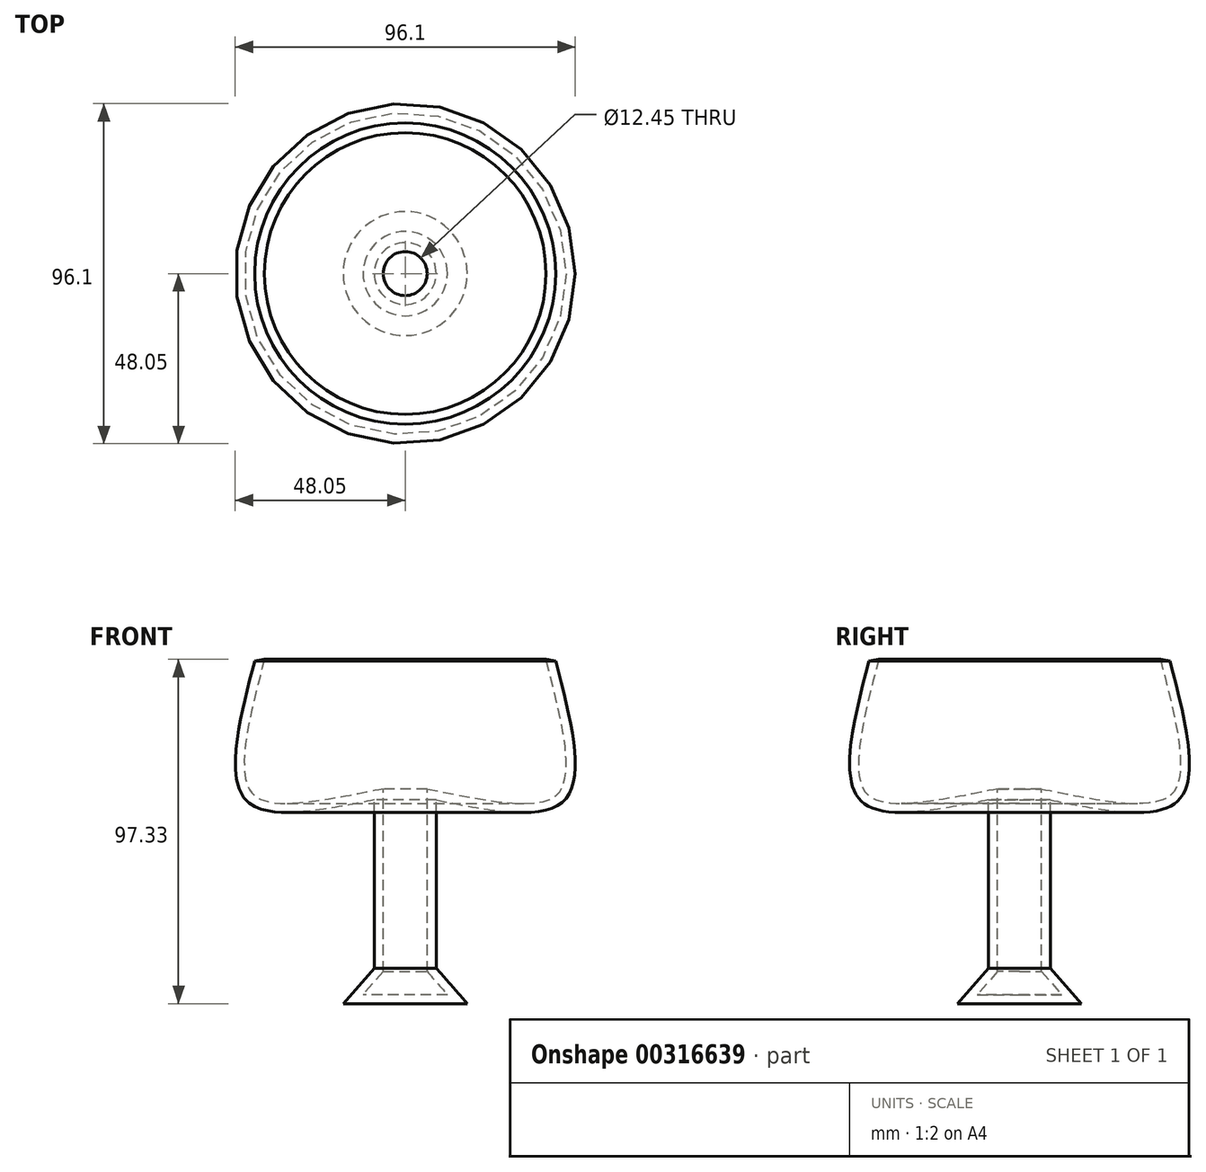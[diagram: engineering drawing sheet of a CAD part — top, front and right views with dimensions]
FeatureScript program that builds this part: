
annotation { "Feature Type Name" : "Feature", "Feature Type Description" : "" }
export const myFeature = defineFeature(function(context is Context, id is Id, definition is map)
    precondition{}
    {
        {
            var Q0;
            Q0=qCreatedBy(makeId("Front.planeOp"),FACE);
            var sketch = newSketch(context, id + "F0", { "sketchPlane" : qUnion([Q0])});
            skLineSegment(sketch, "E0", {"start": v(0, 0) * mm, "end": v(0, 104.74) * mm, "construction": true});
            skLineSegment(sketch, "E1", {"start": v(0, 0) * mm, "end": v(-17.53, 0) * mm});
            skLineSegment(sketch, "E2", {"start": v(-17.53, 0) * mm, "end": v(-8.76, 10.02) * mm});
            skPoint(sketch, "E2.endSnap0", {"position": v(-8.76, 0) * mm});
            skLineSegment(sketch, "E3", {"start": v(-8.76, 10.02) * mm, "end": v(-8.76, 57.59) * mm});
            skFitSpline(sketch, "E4", {"points": [v(-8.76, 57.59) * mm, v(-45.07, 57.59) * mm, v(-42.56, 96.81) * mm], "startDerivative": vector(-93.44, -18.85) * mm, "endDerivative": vector(25.05, 96.54) * mm});
            skLineSegment(sketch, "E5", {"start": v(-42.56, 96.81) * mm, "end": v(0, 104.74) * mm});
            skLineSegment(sketch, "E6", {"start": v(0, 104.74) * mm, "end": v(0, 0) * mm});
            skSolve(sketch);
        }
        {
            var Q0;
            Q0 = qSketchRegion(id + "F0", true);
            var Q1;
            Q1=sQuery(id+"F0.wireOp",EDGE,"E6");
            revolve(context, id + "F1", {"entities" : qUnion([Q0]), "axis" : qUnion([Q1]), "revolveType" : RevolveType.FULL});
        }
        {
            var Q0;
            Q0=makeQuery(id+"F1.opRevolve","SWEPT_FACE",FACE,{"disambiguationData":[OSD([sQuery(id+"F0.wireOp",EDGE,"E5")])]});
            shell(context, id + "F2", {"entities" : qUnion([Q0]), "thickness" : 2.54 * mm});
        }
    });
